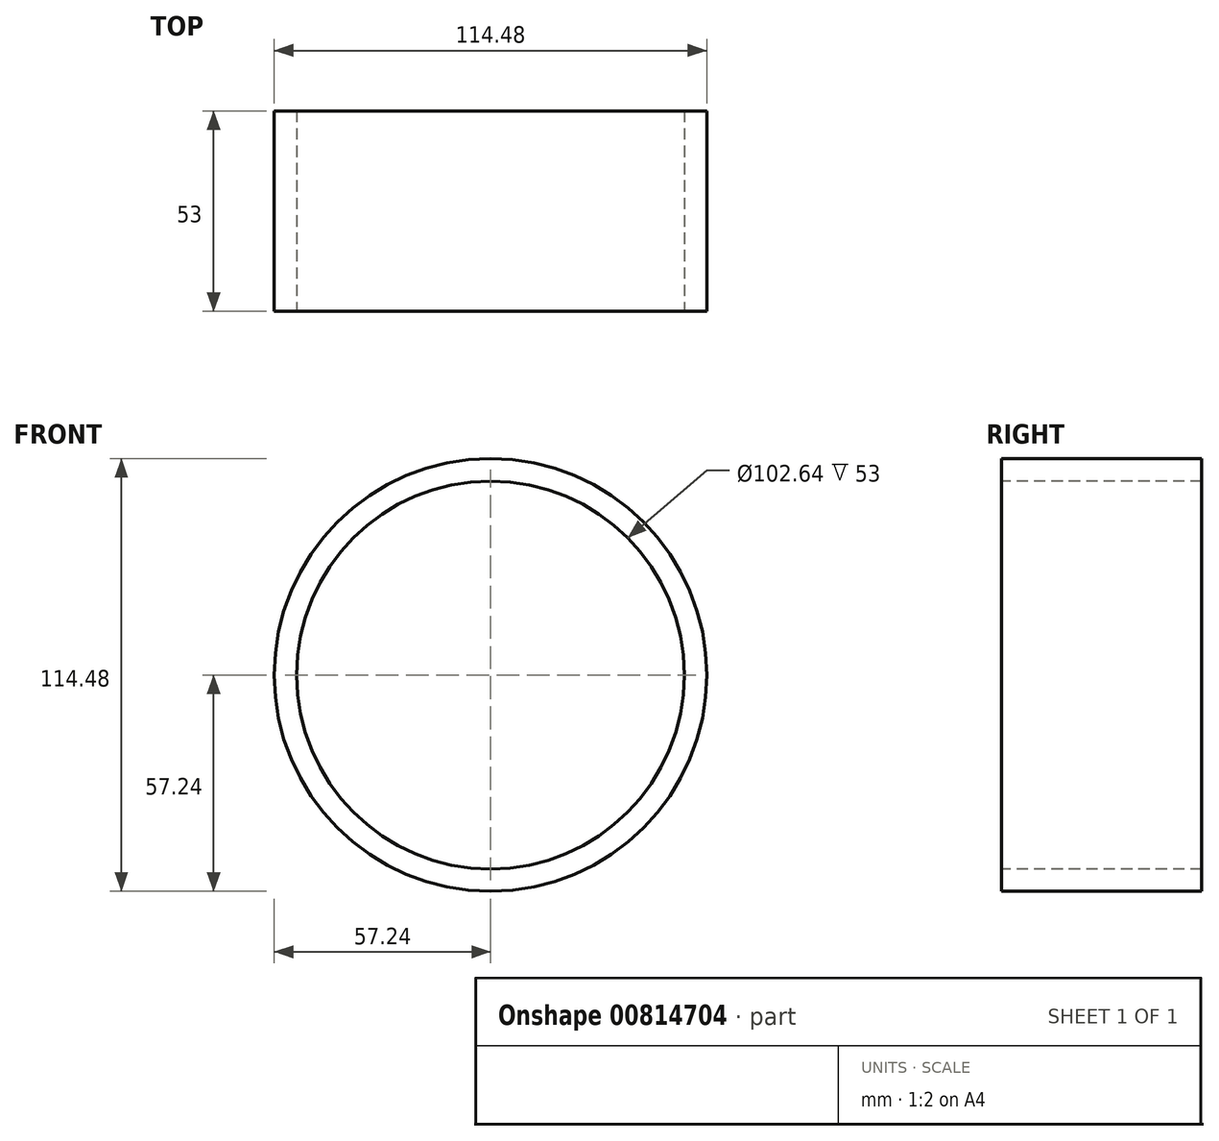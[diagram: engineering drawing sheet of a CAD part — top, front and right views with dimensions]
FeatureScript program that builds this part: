
annotation { "Feature Type Name" : "Feature", "Feature Type Description" : "" }
export const myFeature = defineFeature(function(context is Context, id is Id, definition is map)
    precondition{}
    {
        {
            var Q0;
            Q0=qCreatedBy(makeId("Front.planeOp"),FACE);
            var sketch = newSketch(context, id + "F0", { "sketchPlane" : qUnion([Q0])});
            skCircle(sketch, "E0", {"center": v(0, 0) * mm, "radius": 57.24 * mm});
            skCircle(sketch, "E1", {"center": v(0, 0) * mm, "radius": 51.32 * mm});
            skSolve(sketch);
        }
        {
            var Q0;
            Q0=makeQuery(id+"F0.imprint","IMPRINT",FACE,{"disambiguationData":[TD([[makeQuery(id+"F0.imprint","IMPRINT",EDGE,{"derivedFrom":sQuery(id+"F0.wireOp",EDGE,"E0")}),1.0]])]});
            extrude(context, id + "F1", {"entities" : qUnion([Q0]), "oppositeDirection" : true, "depth" : 53 * mm, "offsetDistance" : 25 * mm});
        }
    });
